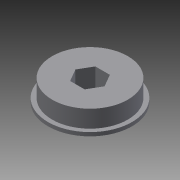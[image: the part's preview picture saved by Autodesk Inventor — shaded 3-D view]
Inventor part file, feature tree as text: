
AUTODESK INVENTOR PART (.ipt)
format: ipt  version: 2014 SP1 (Build 180222100, 222)  size: 100,864 bytes
history: native  units: in
note: dims shown in document units (in); Inventor stores cm internally (conversion verified against a paired STEP export)
features: extrude x2, sketch x2
ambient origin geometry x8: Origin, YZ Plane, XZ Plane, XY Plane, X Axis, Y Axis, Z Axis, Center Point
bodies: Solid1 (feature_tree)
feature tree (4):
  extrude  "Extrusion1"  Depth=0.055in TaperAngle=0.0deg
  extrude  "Extrusion2"  Depth=0.257in TaperAngle=0.0deg
  sketch  "Sketch1"  dims[d0=1.25in d4=0.055in d5=0.0in]
  sketch  "Sketch2"  dims[d6=1.125in d7=0.257in d8=0.0in d9=0.375in]
